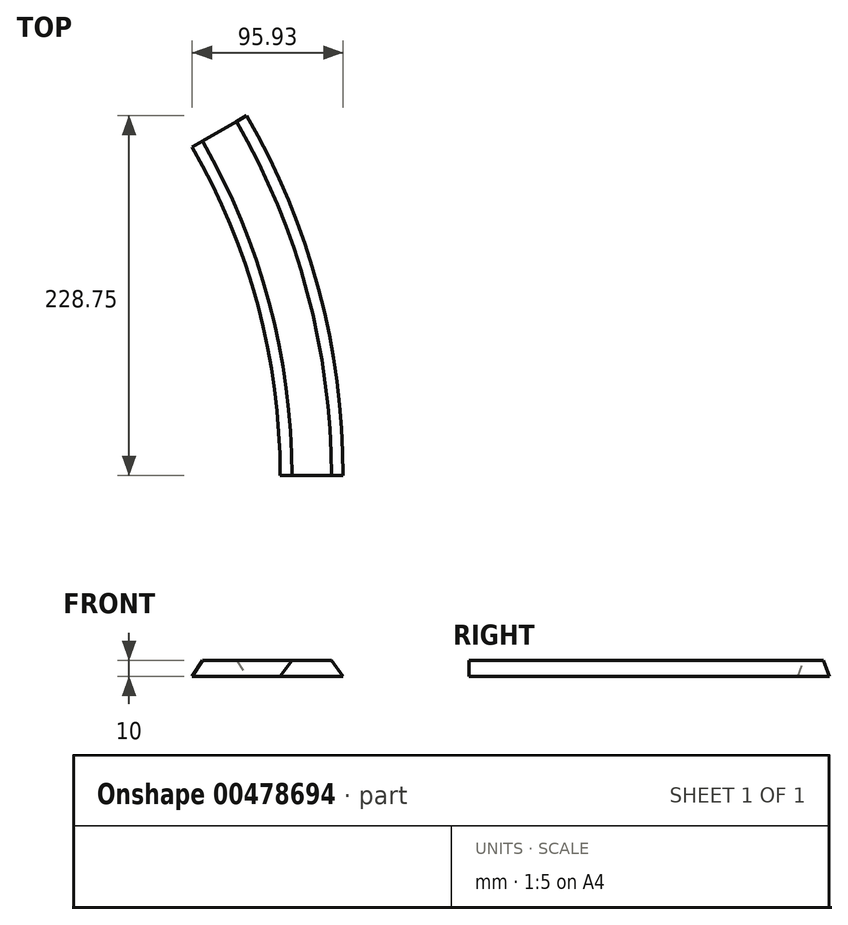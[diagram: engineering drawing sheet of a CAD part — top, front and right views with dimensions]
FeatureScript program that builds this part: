
annotation { "Feature Type Name" : "Feature", "Feature Type Description" : "" }
export const myFeature = defineFeature(function(context is Context, id is Id, definition is map)
    precondition{}
    {
        {
            var Q0;
            Q0=qCreatedBy(makeId("Front.planeOp"),FACE);
            var sketch = newSketch(context, id + "F0", { "sketchPlane" : qUnion([Q0])});
            skLineSegment(sketch, "E0", {"start": v(-20, 0) * mm, "end": v(-12.5, 10) * mm});
            skLineSegment(sketch, "E1", {"start": v(-12.5, 10) * mm, "end": v(12.5, 10) * mm});
            skLineSegment(sketch, "E2", {"start": v(12.5, 10) * mm, "end": v(20, 0) * mm});
            skLineSegment(sketch, "E3", {"start": v(20, 0) * mm, "end": v(-20, 0) * mm});
            skLineSegment(sketch, "E4", {"start": v(0, 0) * mm, "end": v(0, 30.14) * mm, "construction": true});
            skSolve(sketch);
        }
        {
            var Q0;
            Q0=qCreatedBy(makeId("Top.planeOp"),FACE);
            var sketch = newSketch(context, id + "F1", { "sketchPlane" : qUnion([Q0])});
            skArc(sketch, "E5", {"start": v(0, 0) * mm, "mid": v(-14.9, 113.23) * mm, "end": v(-58.61, 218.75) * mm});
            skLineSegment(sketch, "E6", {"start": v(-437.5, 0) * mm, "end": v(-58.61, 218.75) * mm, "construction": true});
            skLineSegment(sketch, "E7", {"start": v(-437.5, 0) * mm, "end": v(0, 0) * mm, "construction": true});
            skSolve(sketch);
        }
        {
            var Q0;
            Q0=qSketchRegion(id+"F0",true);
            var Q1;
            Q1=qConstructionFilter(qBodyType(qCreatedBy(id+"F1",EDGE),BodyType.WIRE),ConstructionObject.NO);
            sweep(context, id + "F2", {"profiles" : qUnion([Q0]), "path" : qUnion([Q1])});
        }
    });
